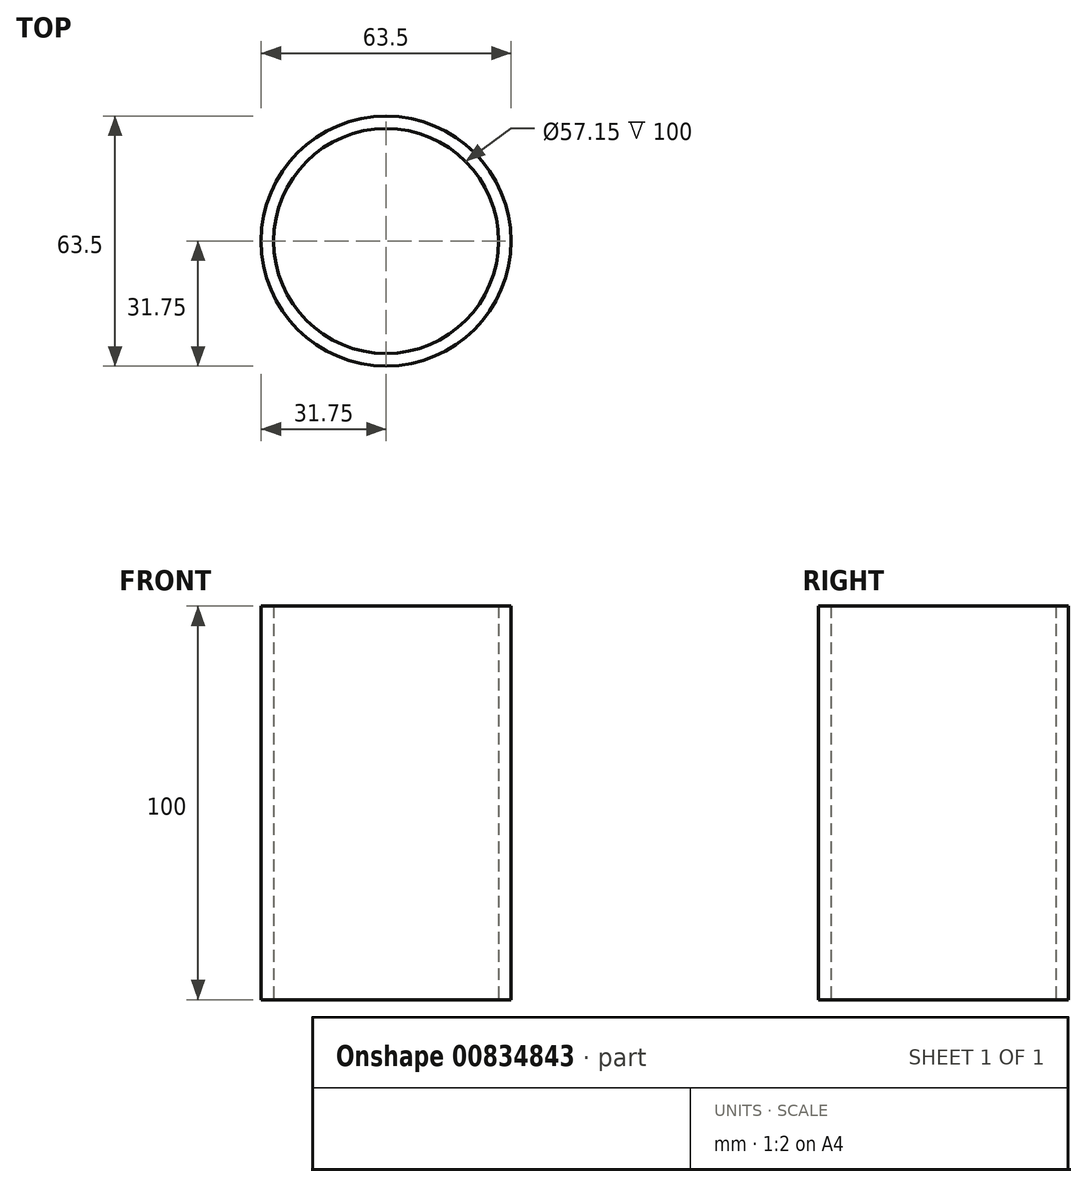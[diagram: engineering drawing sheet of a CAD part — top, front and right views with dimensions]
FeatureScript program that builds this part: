
annotation { "Feature Type Name" : "Feature", "Feature Type Description" : "" }
export const myFeature = defineFeature(function(context is Context, id is Id, definition is map)
    precondition{}
    {
        {
            var Q0;
            Q0=qCreatedBy(makeId("Top.planeOp"),FACE);
            var sketch = newSketch(context, id + "F0", { "sketchPlane" : qUnion([Q0])});
            skCircle(sketch, "E0", {"center": v(0, 0) * mm, "radius": 31.75 * mm});
            skCircle(sketch, "E1", {"center": v(0, 0) * mm, "radius": 28.57 * mm});
            skSolve(sketch);
        }
        {
            var Q0;
            Q0 = qSketchRegion(id + "F0", true);
            extrude(context, id + "F1", {"entities" : qUnion([Q0]), "depth" : 100 * mm, "offsetDistance" : 25 * mm});
        }
    });
